# Revit family: 6 inches 45 degree corner form pp
name_source: partatom
category: Specialty Equipment
revit_build: Autodesk Revit 2015 (Build: 20140606_1530(x64)
units: mm (PartAtom-declared; Revit-internal decimal feet)

## types (1)
- 6" Corner Form 45-degree
    BIMobject category = External Walls
    BIMobject category code = walls-external
    BIMobject main category = Walls
    BIMobject main category code = walls
    Brand url = http://buildblock.com
    Date of publishing = 9/14/2018
    Default Elevation = 48"
    Description = BuildBlock Insulating Concrete Forms
    Design country = United States
    Edition number = 1
    Foam Material = Expanded_Polystyrene-BuildBlock-White
    IFC Classification = Wall
    Installation instructions = http://buildblock.com
    Length = 48"
    Manufacturer = BuildBlock Building Systems LLC
    Manufacturer country = United States
    Manufacturer name = BuildBlock Building Systems, LLC
    Masterformat 2014 Code = 03 11 19
    Masterformat 2014 Description = Insulating Concrete Forming
    Material main = Polystyrene (EPS)
    Material secondary = Polypropylene
    Model = 6" Corner Form 45-degree
    Nominal height = 16"
    Nominal width = 48"
    OmniClass Code = 23-13 31 17 17
    OmniClass Description = Insulated Concrete Forms
    Product Guid = 71bc112b-be75-4e2f-af52-aba8935fba7f
    Product SKU = buildblock-45-degree-corners-6
    Product certification = http://buildblock.com
    Product data url = https://bimobject.com
    Product family = Building materials
    Product group = External wall systems
    Product url = http://buildblock.com
    QR code = http://bimobject.com
    Technical description = http://buildblock.com
    Ties Material = Polypropylene_(Recycled)-Buildblock-Black
    UNSPSC Code = 3013
    URL = http://buildblock.com
    Uniclass 1.4 Code = L32233
    Uniclass 1.4 Description = Insulated blocks
    Uniclass 2.0 Code = SS-25-25
    Uniclass 2.0 Description = Wall Lining Systems
    Uniclass 2015 Code = Pr_20_93_52_42
    Uniclass 2015 Name = Insulated concrete blocks
    Uniformat II Code = B2010
    Uniformat II Description = Exterior Walls
    Weight Net (Kg) = 7
    Width = 11"
    Youtube clip = https://youtu.be

## geometry (parser evidence)
native form markers: Sweep x5
no freeform markers — native parametric forms only
